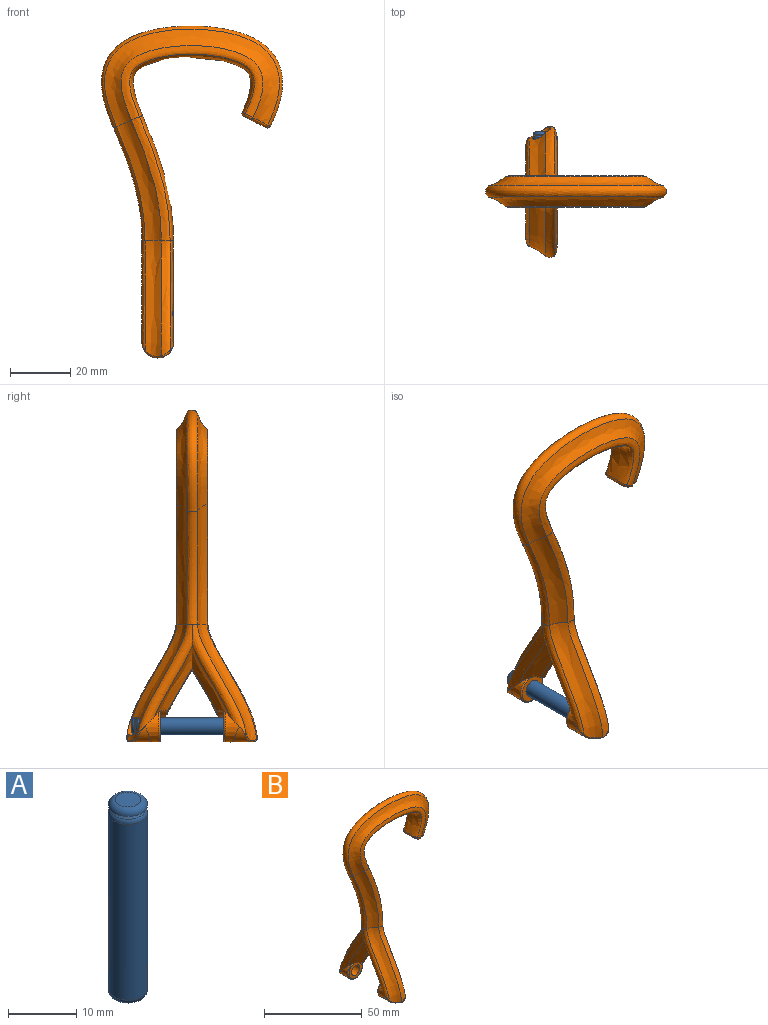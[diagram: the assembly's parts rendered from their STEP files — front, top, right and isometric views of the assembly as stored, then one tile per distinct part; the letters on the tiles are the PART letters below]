
ASSEMBLY  parts=2 mates=1
PART A: 9 faces, bbox 6.2x6.2x35 mm
  f0: cylinder r=2.88mm len=31.59mm, axis (0,0,-1), area 570.6mm2, adj f5,f6
  f1: plane 3.75x3.75mm, normal (0,0,-1), area 11mm2, adj f6
  f2: plane 5.75x5.75mm, normal (0,0,-1), area 8.5mm2, adj f7,f8
  f3: cone r=1.88mm half-angle=45deg, axis (0,0,-1), area 7.8mm2, adj f5,f8
  f4: plane 3.75x3.75mm, normal (0,0,1), area 11mm2, adj f7
  f5: torus R=1.88mm, axis (0,0,-1), area 13.7mm2, adj f0,f3
  f6: torus R=1.88mm, axis (0,0,1), area 24.8mm2, adj f0,f1
  f7: torus R=1.88mm, axis (0,0,1), area 24.8mm2, adj f2,f4
  f8: torus R=2.36mm, axis (0,0,-1), area 6.6mm2, adj f2,f3
PART B: 55 faces, bbox 61.3x44.1x111.1 mm
  f0: bspline ~39.3x26.5mm, area 344.8mm2, adj f7,f11,f12,f18,f26,f30,f31,f36
  f1: bspline ~24.01x13.19mm, area 51.7mm2, adj f3,f7,f12,f32
  f2: cylinder r=3mm len=6mm, axis (0,-1,0), area 61.9mm2, adj f29,f33,f35
  f3: bspline ~30.45x17.82mm, area 137.8mm2, adj f1,f4,f8,f32,f33,f34,f48
  f4: bspline ~39.28x20.18mm, area 153.6mm2, adj f3,f5,f9,f15,f27,f34,f37,f38
  f5: bspline ~39.27x19.66mm, area 264.1mm2, adj f4,f6,f16,f38
  f6: bspline ~39.25x17.04mm, area 123.7mm2, adj f5,f7,f17,f38,f40
  f7: bspline ~39.3x26.5mm, area 344.8mm2, adj f0,f1,f6,f18,f27,f32,f33,f34
  f8: bspline ~30.45x17.82mm, area 137.8mm2, adj f3,f9,f12,f30,f31,f36,f47
  f9: bspline ~39.28x20.18mm, area 153.6mm2, adj f4,f8,f10,f15,f26,f36,f41,f43
  f10: bspline ~39.27x19.66mm, area 242.4mm2, adj f9,f11,f14,f28,f42,f43
  f11: bspline ~39.25x17.04mm, area 116mm2, adj f0,f10,f19,f28,f42,f45
  f12: bspline ~24.01x13.19mm, area 51.7mm2, adj f0,f1,f8,f31
  f13: plane 8.62x7.56mm, normal (-0.46,0,-0.89), area 44mm2, adj f49,f50,f51,f52,f53,f54
  f14: bspline ~39.88x15.03mm, area 259.7mm2, adj f10,f15,f19,f20
  f15: bspline ~37.72x10.96mm, area 171.5mm2, adj f4,f9,f14,f16,f21
  f16: bspline ~39.88x15.03mm, area 259.7mm2, adj f5,f15,f17,f22
  f17: bspline ~41.02x12.89mm, area 125.3mm2, adj f6,f16,f18,f23
  f18: bspline ~41.53x11.53mm, area 451.4mm2, adj f0,f7,f17,f19,f24
  f19: bspline ~41.02x12.89mm, area 125.3mm2, adj f11,f14,f18,f25
  f20: bspline ~58.25x32.84mm, area 609.5mm2, adj f14,f21,f25,f51,f53
  f21: bspline ~61.32x35.06mm, area 480.9mm2, adj f15,f20,f22,f51
  f22: bspline ~58.25x32.84mm, area 609.5mm2, adj f16,f21,f23,f49,f51
  f23: bspline ~47.29x24.86mm, area 234.4mm2, adj f17,f22,f24,f49,f50
  f24: bspline ~41.51x20.83mm, area 730.5mm2, adj f18,f23,f25,f52
  f25: bspline ~47.29x24.86mm, area 234.4mm2, adj f19,f20,f24,f53,f54
  f26: cylinder r=5.25mm len=10.5mm, axis (0,-1,0), area 94.8mm2, adj f0,f9,f36,f41,f43,f45,f46
  f27: cylinder r=5.25mm len=10.5mm, axis (0,-1,0), area 94.8mm2, adj f4,f7,f34,f37,f38,f39,f40
  f28: cylinder r=3mm len=10.93mm, axis (0,-1,0), area 169.4mm2, adj f10,f11,f30,f42
  f29: plane 6x6mm, normal (0,1,0), area 28.3mm2, adj f2
  f30: plane 10.02x9.55mm, normal (0,-1,0), area 46.3mm2, adj f0,f8,f28,f31,f47
  f31: cylinder r=5.25mm len=6.25mm, axis (0,-1,0), area 11.2mm2, adj f0,f8,f12,f30
  f32: cylinder r=5.25mm len=6.25mm, axis (0,-1,0), area 11.2mm2, adj f1,f3,f7,f33
  f33: plane 10.02x9.55mm, normal (0,1,0), area 46.3mm2, adj f2,f3,f7,f32,f35,f48
  f34: extruded ~10.49x10.03mm, area 52.1mm2, adj f3,f4,f7,f27,f48
  f35: extruded ~6x5.63mm, area 22.9mm2, adj f2,f33
  f36: extruded ~10.49x10.03mm, area 52.4mm2, adj f0,f8,f9,f26,f47
  f37: bspline ~2.86x2.48mm, area 0.7mm2, adj f4,f27,f38
  f38: bspline ~6.67x4.26mm, area 6mm2, adj f4,f5,f6,f27,f37,f40
  f39: bspline ~5.77x3.15mm, area 0.9mm2, adj f7,f27,f40
  f40: bspline ~3.42x2.46mm, area 2.8mm2, adj f6,f27,f38,f39
  f41: bspline ~2.89x2.5mm, area 0.7mm2, adj f9,f26,f43
  f42: bspline ~3.14x0.51mm, area 0.5mm2, adj f10,f11,f28,f44
  f43: bspline ~6.62x4.24mm, area 5.9mm2, adj f9,f10,f26,f41,f44
  f44: sphere r=0.5mm, area 0.2mm2, adj f42,f43,f45
  f45: bspline ~3.42x2.46mm, area 2.7mm2, adj f11,f26,f44,f46
  f46: bspline ~5.73x3.1mm, area 0.9mm2, adj f0,f26,f45
  f47: bspline ~10.51x10.42mm, area 18.7mm2, adj f0,f8,f30,f36
  f48: bspline ~10.52x10.41mm, area 18.7mm2, adj f3,f7,f33,f34
  f49: bspline ~7.08x5.2mm, area 10.2mm2, adj f13,f22,f23,f50,f51
  f50: bspline ~3.44x2.42mm, area 3.9mm2, adj f13,f23,f49,f52
  f51: bspline ~4.3x2.34mm, area 5.6mm2, adj f13,f20,f21,f22,f49,f53
  f52: bspline ~10.2x1.73mm, area 15.3mm2, adj f13,f24,f50,f54
  f53: bspline ~7.35x4.68mm, area 10.2mm2, adj f13,f20,f25,f51,f54
  f54: bspline ~3.44x2.42mm, area 3.9mm2, adj f13,f25,f52,f53
PLACE A rot(axis=(-1,0,0),90deg) t=(18.01,-5.16,-21.36)mm
PLACE B t=(19.26,9.84,12.64)mm
MATE fastened A.f0 <-> B.f2  axis (0,-1,0) through (18.01,-5.16,-21.36)mm
